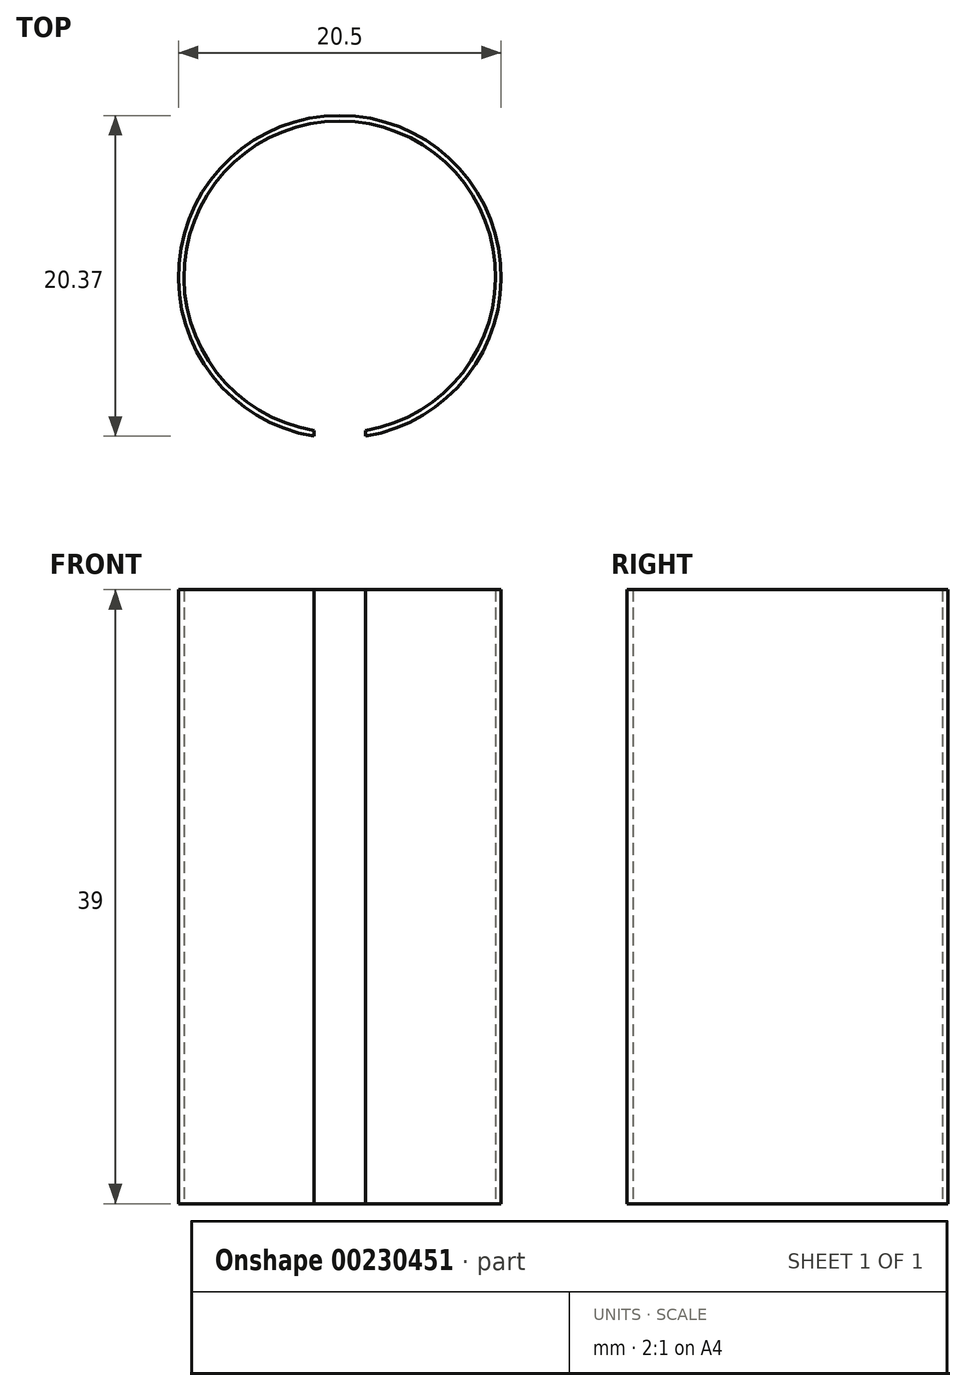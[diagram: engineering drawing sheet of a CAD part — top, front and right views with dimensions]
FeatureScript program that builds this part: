
annotation { "Feature Type Name" : "Feature", "Feature Type Description" : "" }
export const myFeature = defineFeature(function(context is Context, id is Id, definition is map)
    precondition{}
    {
        {
            var Q0;
            Q0=qCreatedBy(makeId("Top.planeOp"),FACE);
            var sketch = newSketch(context, id + "F0", { "sketchPlane" : qUnion([Q0])});
            skArc(sketch, "E0", {"start": v(1.65, -10.12) * mm, "mid": v(0, 10.25) * mm, "end": v(-1.65, -10.12) * mm});
            skArc(sketch, "E1", {"start": v(1.65, -9.76) * mm, "mid": v(0, 9.9) * mm, "end": v(-1.65, -9.76) * mm});
            skLineSegment(sketch, "E2", {"start": v(1.65, -9.76) * mm, "end": v(1.65, -10.12) * mm});
            skLineSegment(sketch, "E3", {"start": v(-1.65, -9.76) * mm, "end": v(-1.65, -10.12) * mm});
            skPoint(sketch, "E4.end.orphan", {"position": v(-1.65, 0) * mm});
            skPoint(sketch, "E5.end.orphan", {"position": v(1.65, 0) * mm});
            skSolve(sketch);
        }
        {
            var Q0;
            Q0=makeQuery(id+"F0.imprint","IMPRINT",FACE,{"disambiguationData":[TD([[makeQuery(id+"F0.imprint","IMPRINT",EDGE,{"derivedFrom":sQuery(id+"F0.wireOp",EDGE,"E0")}),1.0]])]});
            extrude(context, id + "F1", {"entities" : qUnion([Q0]), "depth" : 39 * mm});
        }
        {
            var Q0;
            Q0=qCreatedBy(makeId("Right.planeOp"),FACE);
            var sketch = newSketch(context, id + "F2", { "sketchPlane" : qUnion([Q0])});
            skCircle(sketch, "E6", {"center": v(0, 0) * mm, "radius": 5 * mm});
            skLineSegment(sketch, "E7", {"start": v(0, 0) * mm, "end": v(0, 28) * mm});
            skCircle(sketch, "E8", {"center": v(0, 28) * mm, "radius": 5 * mm});
            skSolve(sketch);
        }
        {
            var Q0;
            Q0=sQuery(id+"F2.wireOp",EDGE,"E8");
            extrude(context, id + "F3", {"bodyType" : ToolBodyType.SURFACE, "surfaceEntities" : qUnion([Q0]), "endBound" : BoundingType.THROUGH_ALL, "depth" : 25 * mm});
        }
    });
